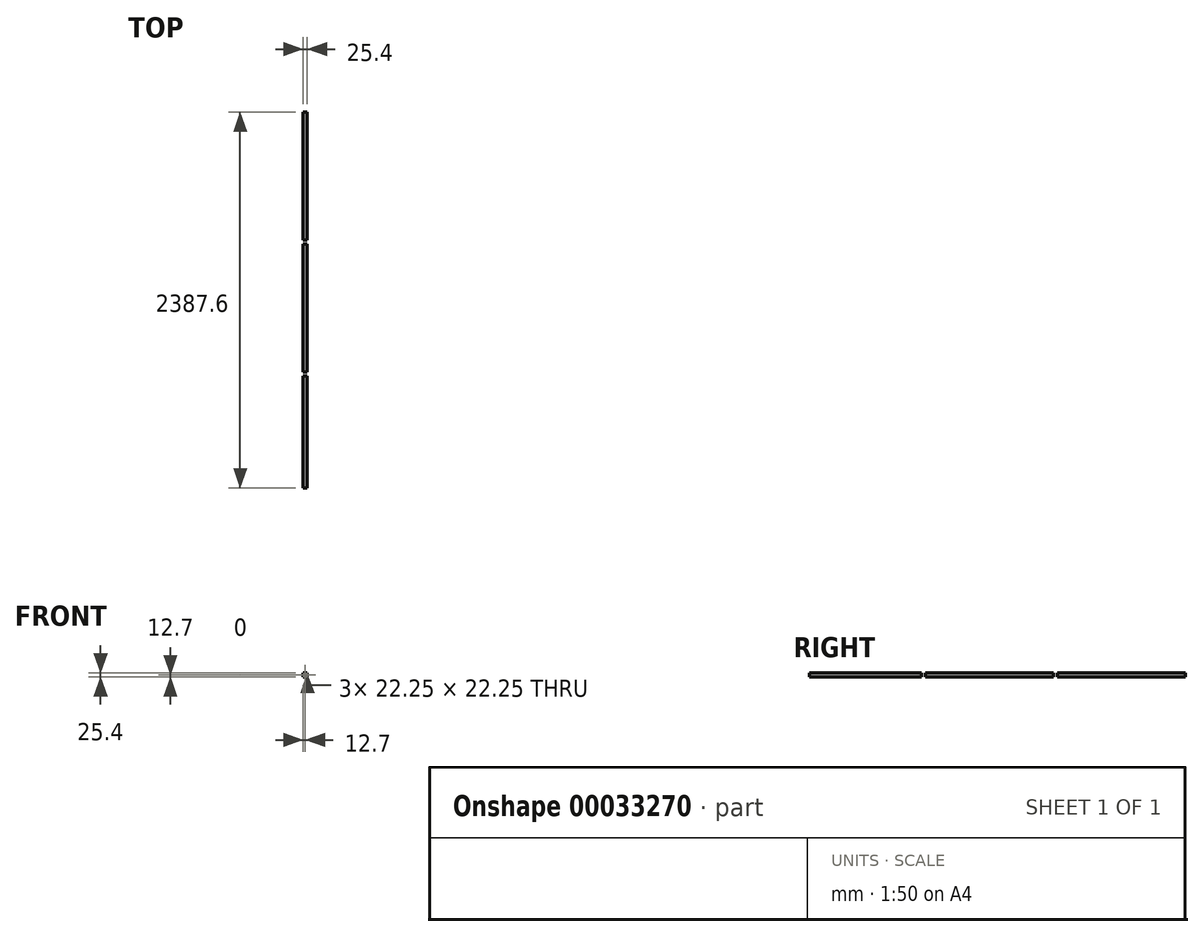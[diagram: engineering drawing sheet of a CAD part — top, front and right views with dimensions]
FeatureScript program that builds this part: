
annotation { "Feature Type Name" : "Feature", "Feature Type Description" : "" }
export const myFeature = defineFeature(function(context is Context, id is Id, definition is map)
    precondition{}
    {
        {
            var Q0;
            Q0=qCreatedBy(makeId("Front.planeOp"),FACE);
            var sketch = newSketch(context, id + "F0", { "sketchPlane" : qUnion([Q0])});
            skLineSegment(sketch, "E0.rect.bottom", {"start": v(-12.7, 12.7) * mm, "end": v(12.7, 12.7) * mm});
            skLineSegment(sketch, "E0.rect.top", {"start": v(-12.7, -12.7) * mm, "end": v(12.7, -12.7) * mm});
            skLineSegment(sketch, "E0.rect.left", {"start": v(-12.7, 12.7) * mm, "end": v(-12.7, -12.7) * mm});
            skLineSegment(sketch, "E0.rect.right", {"start": v(12.7, 12.7) * mm, "end": v(12.7, -12.7) * mm});
            skPoint(sketch, "E0.rect.middle", {"position": v(0, 0) * mm});
            skLineSegment(sketch, "E1.rect.bottom", {"start": v(-11.13, 11.13) * mm, "end": v(11.13, 11.13) * mm});
            skLineSegment(sketch, "E1.rect.top", {"start": v(-11.13, -11.13) * mm, "end": v(11.13, -11.13) * mm});
            skLineSegment(sketch, "E1.rect.left", {"start": v(-11.13, 11.13) * mm, "end": v(-11.13, -11.13) * mm});
            skLineSegment(sketch, "E1.rect.right", {"start": v(11.13, 11.13) * mm, "end": v(11.13, -11.13) * mm});
            skSolve(sketch);
        }
        {
            var Q0;
            Q0 = qSketchRegion(id + "F0", true);
            extrude(context, id + "F1", {"entities" : qUnion([Q0]), "depth" : 812.8 * mm});
        }
        {
            var Q0;
            Q0=makeQuery(id+"F1.opExtrude","CAP_FACE",FACE,{"disambiguationData":[OSD([sQuery(id+"F0.wireOp",EDGE,"E0.rect.bottom"),sQuery(id+"F0.wireOp",EDGE,"E0.rect.top"),sQuery(id+"F0.wireOp",EDGE,"E0.rect.left"),sQuery(id+"F0.wireOp",EDGE,"E0.rect.right"),sQuery(id+"F0.wireOp",EDGE,"E1.rect.bottom"),sQuery(id+"F0.wireOp",EDGE,"E1.rect.top"),sQuery(id+"F0.wireOp",EDGE,"E1.rect.left"),sQuery(id+"F0.wireOp",EDGE,"E1.rect.right")])],"isStart":false});
            var sketch = newSketch(context, id + "F2", { "sketchPlane" : qUnion([Q0])});
            skLineSegment(sketch, "E2.rect.bottom", {"start": v(-11.13, -11.13) * mm, "end": v(11.13, -11.13) * mm});
            skLineSegment(sketch, "E2.rect.top", {"start": v(-11.13, 11.13) * mm, "end": v(11.13, 11.13) * mm});
            skLineSegment(sketch, "E2.rect.left", {"start": v(-11.13, -11.13) * mm, "end": v(-11.13, 11.13) * mm});
            skLineSegment(sketch, "E2.rect.right", {"start": v(11.13, -11.13) * mm, "end": v(11.13, 11.13) * mm});
            skPoint(sketch, "E2.rect.middle", {"position": v(0, 0) * mm});
            skLineSegment(sketch, "E3.rect.bottom", {"start": v(-12.7, -12.7) * mm, "end": v(12.7, -12.7) * mm});
            skLineSegment(sketch, "E3.rect.top", {"start": v(-12.7, 12.7) * mm, "end": v(12.7, 12.7) * mm});
            skLineSegment(sketch, "E3.rect.left", {"start": v(-12.7, -12.7) * mm, "end": v(-12.7, 12.7) * mm});
            skLineSegment(sketch, "E3.rect.right", {"start": v(12.7, -12.7) * mm, "end": v(12.7, 12.7) * mm});
            skSolve(sketch);
        }
        {
            var Q0;
            Q0 = qSketchRegion(id + "F2", true);
            extrude(context, id + "F3", {"entities" : qUnion([Q0]), "depth" : 838.2 * mm, "hasSecondDirection" : true, "secondDirectionOppositeDirection" : false, "secondDirectionDepth" : 25.4 * mm});
        }
        {
            var Q0;
            Q0=makeQuery(id+"F3.opExtrude","CAP_FACE",FACE,{"disambiguationData":[OSD([sQuery(id+"F2.wireOp",EDGE,"E2.rect.bottom"),sQuery(id+"F2.wireOp",EDGE,"E2.rect.top"),sQuery(id+"F2.wireOp",EDGE,"E2.rect.left"),sQuery(id+"F2.wireOp",EDGE,"E2.rect.right"),sQuery(id+"F2.wireOp",EDGE,"E3.rect.bottom"),sQuery(id+"F2.wireOp",EDGE,"E3.rect.top"),sQuery(id+"F2.wireOp",EDGE,"E3.rect.left"),sQuery(id+"F2.wireOp",EDGE,"E3.rect.right")])],"isStart":false});
            var sketch = newSketch(context, id + "F4", { "sketchPlane" : qUnion([Q0])});
            skLineSegment(sketch, "E4.rect.bottom", {"start": v(11.13, 11.13) * mm, "end": v(-11.13, 11.13) * mm});
            skLineSegment(sketch, "E4.rect.top", {"start": v(11.13, -11.13) * mm, "end": v(-11.13, -11.13) * mm});
            skLineSegment(sketch, "E4.rect.left", {"start": v(11.13, 11.13) * mm, "end": v(11.13, -11.13) * mm});
            skLineSegment(sketch, "E4.rect.right", {"start": v(-11.13, 11.13) * mm, "end": v(-11.13, -11.13) * mm});
            skPoint(sketch, "E4.rect.middle", {"position": v(0, 0) * mm});
            skLineSegment(sketch, "E5.rect.bottom", {"start": v(12.7, 12.7) * mm, "end": v(-12.7, 12.7) * mm});
            skLineSegment(sketch, "E5.rect.top", {"start": v(12.7, -12.7) * mm, "end": v(-12.7, -12.7) * mm});
            skLineSegment(sketch, "E5.rect.left", {"start": v(12.7, 12.7) * mm, "end": v(12.7, -12.7) * mm});
            skLineSegment(sketch, "E5.rect.right", {"start": v(-12.7, 12.7) * mm, "end": v(-12.7, -12.7) * mm});
            skSolve(sketch);
        }
        {
            var Q0;
            Q0 = qSketchRegion(id + "F4", true);
            extrude(context, id + "F5", {"entities" : qUnion([Q0]), "depth" : 736.6 * mm, "hasSecondDirection" : true, "secondDirectionOppositeDirection" : false, "secondDirectionDepth" : 25.4 * mm});
        }
    });
